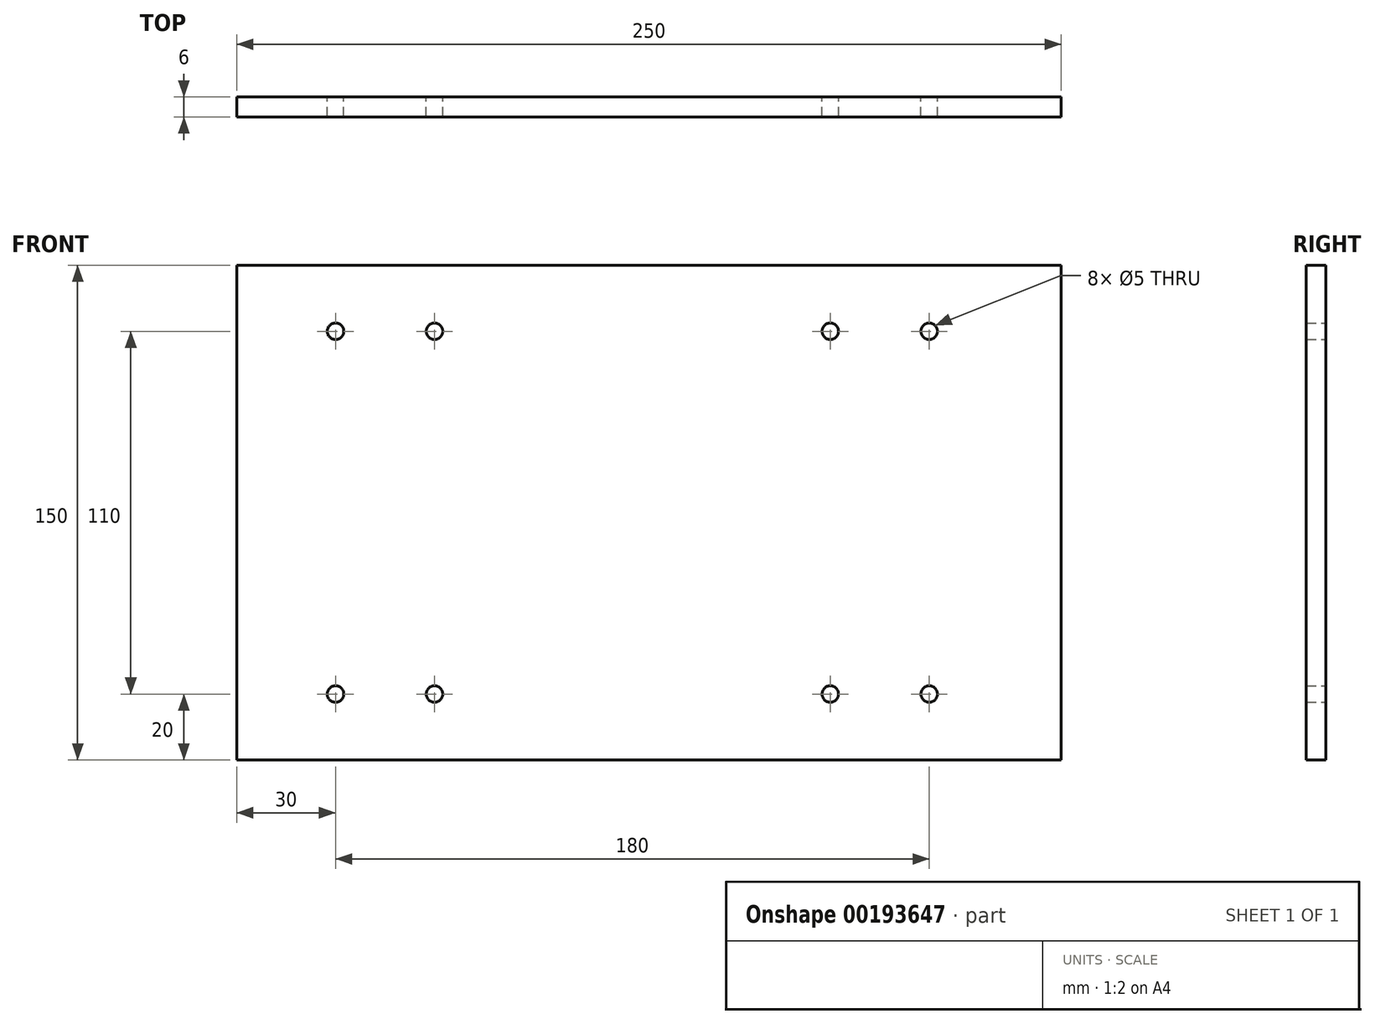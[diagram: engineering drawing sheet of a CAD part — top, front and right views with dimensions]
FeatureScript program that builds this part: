
annotation { "Feature Type Name" : "Feature", "Feature Type Description" : "" }
export const myFeature = defineFeature(function(context is Context, id is Id, definition is map)
    precondition{}
    {
        {
            var Q0;
            Q0=qCreatedBy(makeId("Front.planeOp"),FACE);
            var sketch = newSketch(context, id + "F0", { "sketchPlane" : qUnion([Q0])});
            skLineSegment(sketch, "E0.bottom", {"start": v(-125, 75) * mm, "end": v(125, 75) * mm});
            skLineSegment(sketch, "E0.top", {"start": v(-125, -75) * mm, "end": v(125, -75) * mm});
            skLineSegment(sketch, "E0.left", {"start": v(-125, 75) * mm, "end": v(-125, -75) * mm});
            skLineSegment(sketch, "E0.right", {"start": v(125, 75) * mm, "end": v(125, -75) * mm});
            skPoint(sketch, "E0.middle", {"position": v(0, 0) * mm});
            skCircle(sketch, "E1", {"center": v(-95, 55) * mm, "radius": 2.5 * mm});
            skCircle(sketch, "E2", {"center": v(-65, 55) * mm, "radius": 2.5 * mm});
            skCircle(sketch, "E3", {"center": v(55, 55) * mm, "radius": 2.5 * mm});
            skCircle(sketch, "E4", {"center": v(85, 55) * mm, "radius": 2.5 * mm});
            skCircle(sketch, "E5", {"center": v(85, -55) * mm, "radius": 2.5 * mm});
            skCircle(sketch, "E6", {"center": v(55, -55) * mm, "radius": 2.5 * mm});
            skCircle(sketch, "E7", {"center": v(-95, -55) * mm, "radius": 2.5 * mm});
            skCircle(sketch, "E8", {"center": v(-65, -55) * mm, "radius": 2.5 * mm});
            skSolve(sketch);
        }
        {
            var Q0;
            Q0=makeQuery(id+"F0.imprint","IMPRINT",FACE,{"disambiguationData":[TD([[makeQuery(id+"F0.imprint","IMPRINT",EDGE,{"derivedFrom":sQuery(id+"F0.wireOp",EDGE,"E0.bottom")}),-1.0]])]});
            var Q1;
            Q1 = qSketchRegion(id + "FeA2C1gRDi3TIqN_0", true);
            extrude(context, id + "F1", {"entities" : qUnion([Q0, Q1]), "depth" : 6 * mm});
        }
    });
